# Revit family: Ceiling_Sensor-Wireless_Daylight-Hubbell_Wiring-WLDH
name_source: partatom
category: Lighting Devices
revit_build: Autodesk Revit Architecture 2015 (Build: 20140606_1530(x64)
units: mm (PartAtom-declared; Revit-internal decimal feet)

## types (1)
- WLDH
    Apparent Load = 0.002 VA
    BIMobject category = Controls
    BIMobject category code = electrical-controls
    BIMobject main category = Electrical
    BIMobject main category code = electrical
    Brand url = http://www.hubbell-wiring.com
    Connector Description 1 = Power Supply
    Connector Description 2 = Controls
    Date of publishing = 9/28/2015
    Default Elevation = 48.000"
    Description = Wireless Daylight Sensor
    Device Material = Plastic - Hubbell - White
    Edition number = 1
    Glass = Plastic - Hubbell - Polyethylene
    Load Classification = Lighting
    Manufacturer = Hubbell Wiring Device-Kellems
    Manufacturer name = Hubbell Wiring Device-Kellems
    Model = WLDH
    Nominal height = 0.000"
    Nominal width = 0.000"
    Number of Poles = 1
    Power Factor = 1
    Product Documentation Link = http://ecatalog.hubbell-wiring.com
    Product Guid = 7b345b31-0ae5-449f-82d4-cb18610e7c58
    Product Page URL = http://ecatalog.hubbell-wiring.com
    Product SKU = hubbell-wldh
    Product data url = https://bimobject.com
    Product family = Lighting Controls
    Product group = Ceiling Sensor
    Product url = http://ecatalog.hubbell-wiring.com
    QR code = http://bimobject.com
    Transmitter = Yes
    URL = http://www.hubbell-wiring.com
    Voltage = 3 V
    Weight Net (Kg) = 0

## geometry (parser evidence)
native form markers: Blend x5, Sweep x3
no freeform markers — native parametric forms only
